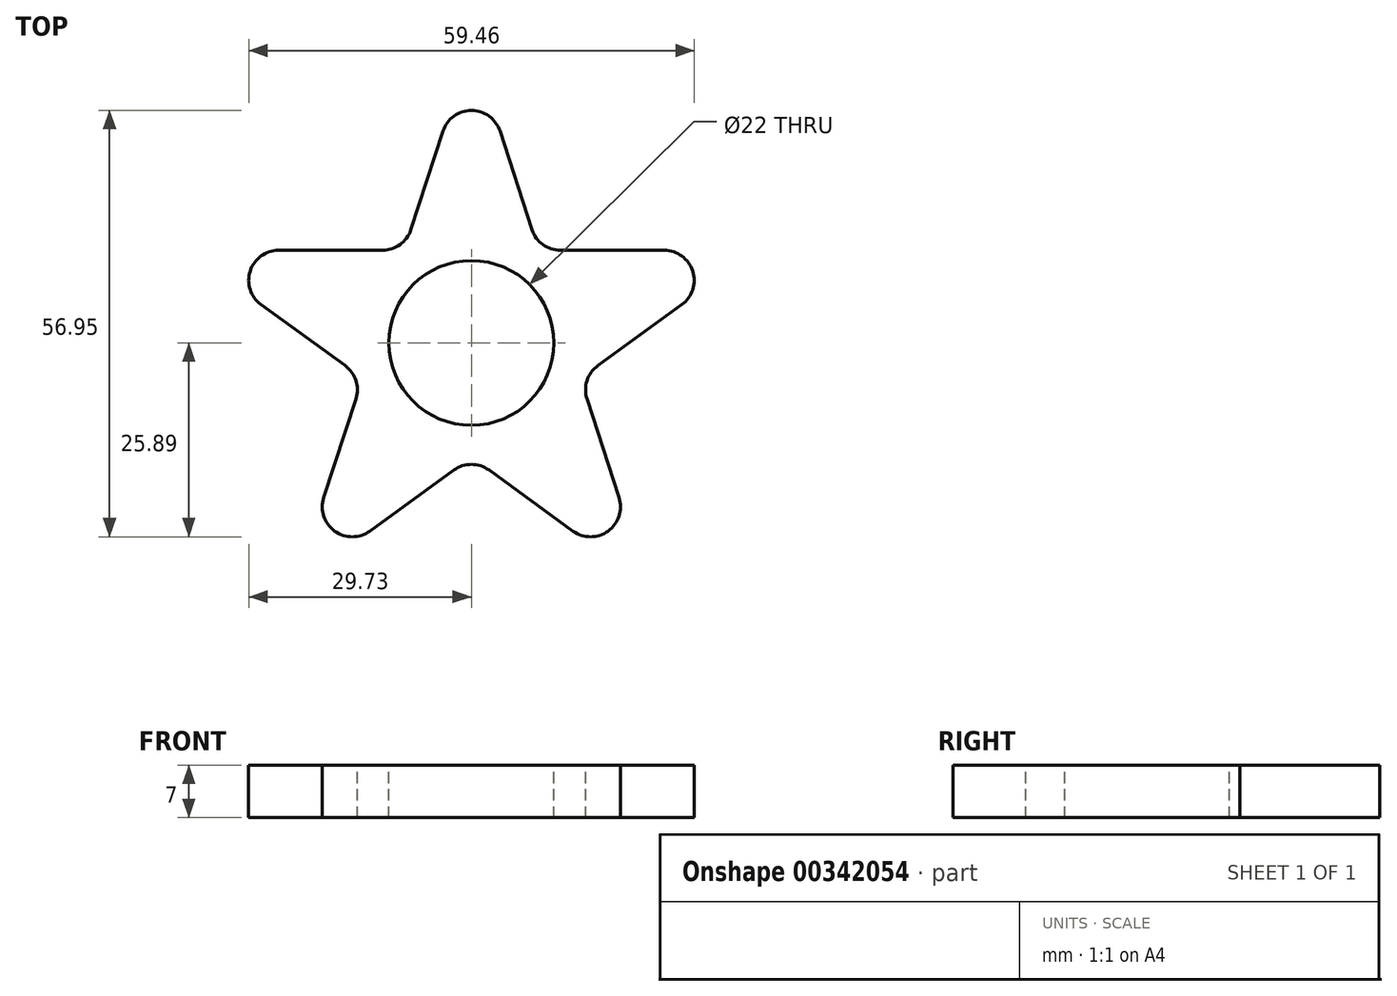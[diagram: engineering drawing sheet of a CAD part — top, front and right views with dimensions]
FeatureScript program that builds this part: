
annotation { "Feature Type Name" : "Feature", "Feature Type Description" : "" }
export const myFeature = defineFeature(function(context is Context, id is Id, definition is map)
    precondition{}
    {
        {
            var Q0;
            Q0=qCreatedBy(makeId("Top.planeOp"),FACE);
            var sketch = newSketch(context, id + "F0", { "sketchPlane" : qUnion([Q0])});
            skCircle(sketch, "E0", {"center": v(0, 0) * mm, "radius": 11 * mm});
            skCircle(sketch, "E1.cCircle", {"center": v(0, 0) * mm, "radius": 40 * mm, "construction": true});
            skLineSegment(sketch, "E2", {"start": v(-3.8, 28.3) * mm, "end": v(-8.08, 15.12) * mm});
            skLineSegment(sketch, "E3", {"start": v(-13.55, -25.12) * mm, "end": v(-2.35, -16.99) * mm});
            skLineSegment(sketch, "E4", {"start": v(25.73, 12.36) * mm, "end": v(11.89, 12.36) * mm});
            skLineSegment(sketch, "E5", {"start": v(-28.08, 5.12) * mm, "end": v(-16.88, -3.01) * mm});
            skLineSegment(sketch, "E6", {"start": v(19.7, -20.65) * mm, "end": v(15.43, -7.49) * mm});
            skLineSegment(sketch, "E7.trimOffspring", {"start": v(-15.43, -7.49) * mm, "end": v(-19.7, -20.65) * mm});
            skLineSegment(sketch, "E8.trimOffspring", {"start": v(-11.89, 12.36) * mm, "end": v(-25.73, 12.36) * mm});
            skLineSegment(sketch, "E9.trimOffspring", {"start": v(8.08, 15.12) * mm, "end": v(3.8, 28.3) * mm});
            skLineSegment(sketch, "E10.trimOffspring", {"start": v(16.88, -3.01) * mm, "end": v(28.08, 5.12) * mm});
            skLineSegment(sketch, "E11.trimOffspring", {"start": v(2.35, -16.99) * mm, "end": v(13.55, -25.12) * mm});
            skPoint(sketch, "E12.visualSharp", {"position": v(-8.98, 12.36) * mm});
            skArc(sketch, "E12.filletArc", {"start": v(-11.89, 12.36) * mm, "mid": v(-9.54, 13.12) * mm, "end": v(-8.08, 15.12) * mm});
            skPoint(sketch, "E13.visualSharp", {"position": v(8.98, 12.36) * mm});
            skArc(sketch, "E13.filletArc", {"start": v(8.08, 15.12) * mm, "mid": v(9.54, 13.12) * mm, "end": v(11.89, 12.36) * mm});
            skPoint(sketch, "E14.visualSharp", {"position": v(14.53, -4.72) * mm});
            skArc(sketch, "E14.filletArc", {"start": v(16.88, -3.01) * mm, "mid": v(15.43, -5.01) * mm, "end": v(15.43, -7.49) * mm});
            skPoint(sketch, "E15.visualSharp", {"position": v(0, -15.28) * mm});
            skArc(sketch, "E15.filletArc", {"start": v(2.35, -16.99) * mm, "mid": v(0, -16.22) * mm, "end": v(-2.35, -16.99) * mm});
            skPoint(sketch, "E16.visualSharp", {"position": v(-14.53, -4.72) * mm});
            skArc(sketch, "E16.filletArc", {"start": v(-15.43, -7.49) * mm, "mid": v(-15.43, -5.01) * mm, "end": v(-16.88, -3.01) * mm});
            skPoint(sketch, "E17.visualSharp", {"position": v(-23.51, -32.36) * mm});
            skArc(sketch, "E17.filletArc", {"start": v(-19.7, -20.65) * mm, "mid": v(-18.25, -25.12) * mm, "end": v(-13.55, -25.12) * mm});
            skPoint(sketch, "E18.visualSharp", {"position": v(-38.04, 12.36) * mm});
            skArc(sketch, "E18.filletArc", {"start": v(-25.73, 12.36) * mm, "mid": v(-29.54, 9.6) * mm, "end": v(-28.08, 5.12) * mm});
            skPoint(sketch, "E19.visualSharp", {"position": v(0, 40) * mm});
            skArc(sketch, "E19.filletArc", {"start": v(3.8, 28.3) * mm, "mid": v(0, 31.06) * mm, "end": v(-3.8, 28.3) * mm});
            skPoint(sketch, "E20.visualSharp", {"position": v(38.04, 12.36) * mm});
            skArc(sketch, "E20.filletArc", {"start": v(28.08, 5.12) * mm, "mid": v(29.54, 9.6) * mm, "end": v(25.73, 12.36) * mm});
            skPoint(sketch, "E21.visualSharp", {"position": v(23.51, -32.36) * mm});
            skArc(sketch, "E21.filletArc", {"start": v(13.55, -25.12) * mm, "mid": v(18.25, -25.12) * mm, "end": v(19.7, -20.65) * mm});
            skSolve(sketch);
        }
        {
            var Q0;
            Q0=makeQuery(id+"F0.imprint","IMPRINT",FACE,{"disambiguationData":[TD([[makeQuery(id+"F0.imprint","IMPRINT",EDGE,{"derivedFrom":sQuery(id+"F0.wireOp",EDGE,"E0")}),-1.0]])]});
            extrude(context, id + "F1", {"entities" : qUnion([Q0]), "oppositeDirection" : true, "depth" : 7 * mm});
        }
    });
